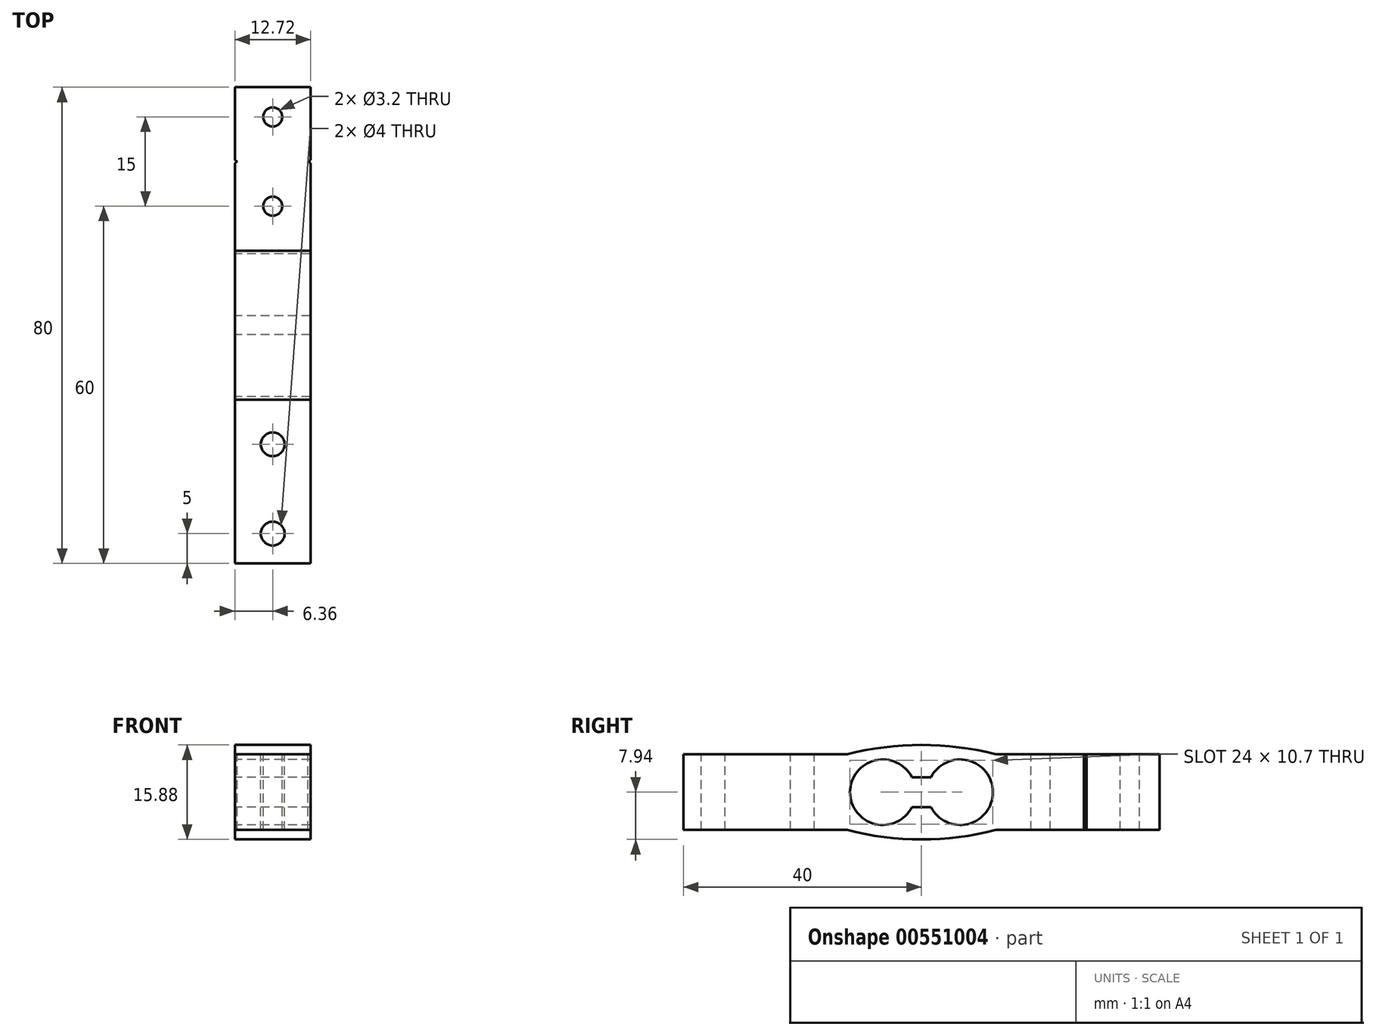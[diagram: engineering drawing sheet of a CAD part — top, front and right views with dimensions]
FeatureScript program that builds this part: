
annotation { "Feature Type Name" : "Feature", "Feature Type Description" : "" }
export const myFeature = defineFeature(function(context is Context, id is Id, definition is map)
    precondition{}
    {
        {
            var Q0;
            Q0=qCreatedBy(makeId("Right.planeOp"),FACE);
            var sketch = newSketch(context, id + "F0", { "sketchPlane" : qUnion([Q0])});
            skLineSegment(sketch, "E0.bottom", {"start": v(40, 6.35) * mm, "end": v(12.5, 6.35) * mm});
            skLineSegment(sketch, "E0.top", {"start": v(40, -6.35) * mm, "end": v(12.5, -6.35) * mm});
            skLineSegment(sketch, "E0.left", {"start": v(40, 6.35) * mm, "end": v(40, -6.35) * mm});
            skLineSegment(sketch, "E0.right", {"start": v(-40, 6.35) * mm, "end": v(-40, -6.35) * mm});
            skArc(sketch, "E1", {"start": v(1.6, -2.5) * mm, "mid": v(12, 0) * mm, "end": v(1.6, 2.5) * mm});
            skArc(sketch, "E2", {"start": v(-1.6, 2.5) * mm, "mid": v(-12, 0) * mm, "end": v(-1.6, -2.5) * mm});
            skLineSegment(sketch, "E3.bottom", {"start": v(1.6, 2.5) * mm, "end": v(-1.6, 2.5) * mm});
            skLineSegment(sketch, "E3.top", {"start": v(1.6, -2.5) * mm, "end": v(-1.6, -2.5) * mm});
            skArc(sketch, "E4", {"start": v(12.5, 6.35) * mm, "mid": v(0, 7.94) * mm, "end": v(-12.5, 6.35) * mm});
            skArc(sketch, "E5", {"start": v(12.5, -6.35) * mm, "mid": v(0, -7.94) * mm, "end": v(-12.5, -6.35) * mm});
            skLineSegment(sketch, "E6.trimOffspring", {"start": v(-12.5, 6.35) * mm, "end": v(-40, 6.35) * mm});
            skLineSegment(sketch, "E7.trimOffspring", {"start": v(-12.5, -6.35) * mm, "end": v(-40, -6.35) * mm});
            skSolve(sketch);
        }
        {
            var Q0;
            Q0=qSketchRegion(id+"F0",true);
            extrude(context, id + "F1", {"entities" : qUnion([Q0]), "endBound" : BoundingType.SYMMETRIC, "depth" : 12.72 * mm});
        }
        {
            var Q0;
            Q0=makeQuery(id+"F1.opExtrude","SWEPT_FACE",FACE,{"disambiguationData":[OSD([sQuery(id+"F0.wireOp",EDGE,"E0.bottom")])]});
            var sketch = newSketch(context, id + "F2", { "sketchPlane" : qUnion([Q0])});
            skCircle(sketch, "E8", {"center": v(0, -20) * mm, "radius": 2 * mm});
            skCircle(sketch, "E9", {"center": v(0, -35) * mm, "radius": 2 * mm});
            skCircle(sketch, "E10.MirrorC", {"center": v(0, 20) * mm, "radius": 1.6 * mm});
            skCircle(sketch, "E11.MirrorC", {"center": v(0, 35) * mm, "radius": 1.6 * mm});
            skLineSegment(sketch, "E12", {"start": v(6.36, 27.75) * mm, "end": v(5.93, 27.5) * mm});
            skLineSegment(sketch, "E13", {"start": v(5.93, 27.5) * mm, "end": v(6.36, 27.25) * mm});
            skLineSegment(sketch, "E14", {"start": v(6.36, 27.25) * mm, "end": v(6.36, 27.75) * mm});
            skLineSegment(sketch, "E15", {"start": v(-6.36, 27.75) * mm, "end": v(-5.93, 27.5) * mm});
            skLineSegment(sketch, "E16", {"start": v(-5.93, 27.5) * mm, "end": v(-6.36, 27.25) * mm});
            skLineSegment(sketch, "E17", {"start": v(-6.36, 27.25) * mm, "end": v(-6.36, 27.75) * mm});
            skLineSegment(sketch, "E18", {"start": v(-5.93, 27.5) * mm, "end": v(5.93, 27.5) * mm, "construction": true});
            skSolve(sketch);
        }
        {
            var Q0;
            Q0=qSketchRegion(id+"F2",true);
            extrude(context, id + "F3", {"entities" : qUnion([Q0]), "operationType" : NewBodyOperationType.REMOVE, "endBound" : BoundingType.THROUGH_ALL, "oppositeDirection" : true, "depth" : 25 * mm});
        }
    });
